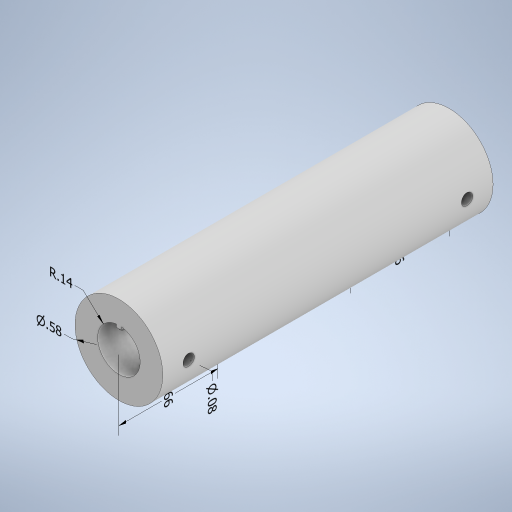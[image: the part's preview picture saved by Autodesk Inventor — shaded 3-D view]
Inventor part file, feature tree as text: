
AUTODESK INVENTOR PART (.ipt)
format: ipt  version: 2023 (Build 270158000, 158)  size: 620,032 bytes
history: native  units: in
note: dims shown in document units (in); Inventor stores cm internally (conversion verified against a paired STEP export)
features: other x7, extrude x4, sketch x4, mirror x1
ambient origin geometry x8: Origin, YZ Plane, XZ Plane, XY Plane, X Axis, Y Axis, Z Axis, Center Point
bodies: Solid1 (feature_tree)
feature tree (16):
  other  "Annotations"
  extrude  "Extrusion1"  Depth=2.1874in TaperAngle=0.0deg
  extrude  "Extrusion2"  Depth=0.6562in TaperAngle=0.0deg
  extrude  "Extrusion3"  Depth=0.9219in
  extrude  "Extrusion5"  Depth=0.1406in
  mirror  "Mirror5"
  sketch  "Sketch1"  dims[d0=0.5813in d1=2.1874in d2=1.083in d3=0.0in d4=0.0in]
  sketch  "Sketch3"  dims[d6=0.2813in d7=0.6562in d8=0.0in]
  sketch  "Sketch4"  dims[d9=0.9219in d10=0.075in]
  sketch  "Sketch6"  dims[d11=0.0in d12=0.0in d17=0.02in d18=0.034in d19=0.0in d20=2.0957in d21=0.3519in d22=0.0022in d23=0.075in d24=0.9394in d25=0.1406in d26=1.3504in d27=0.5813in d28=0.6562in d29=0.6562in d30=2.1369in d31=0.1406in]
  other  "Diameter Dimension 1"
  other  "Radial Dimension 1"
  other  "Diameter Dimension 2"
  other  "Linear Dimension 1"
  other  "Linear Dimension 2"
  other  "Radial Dimension 2"
